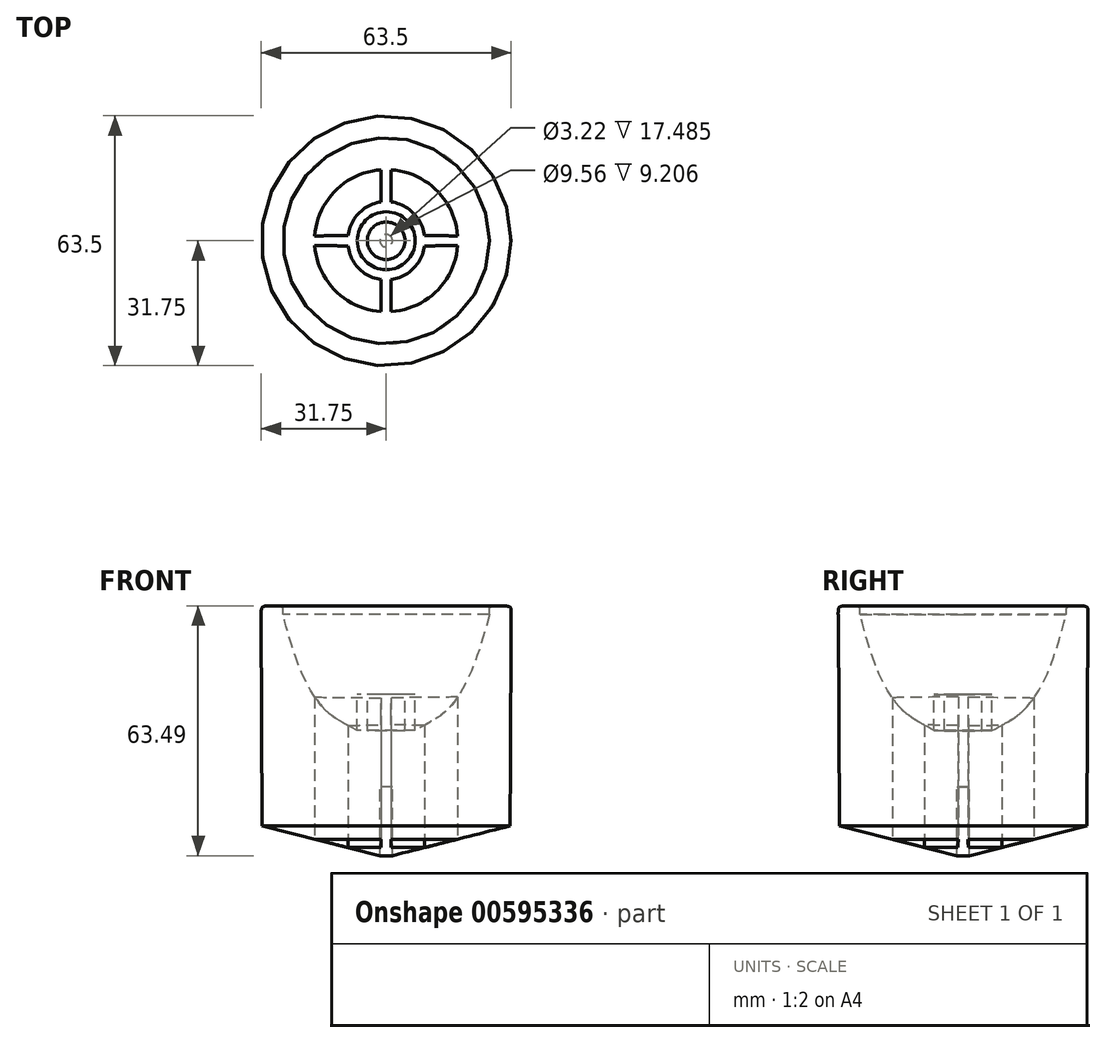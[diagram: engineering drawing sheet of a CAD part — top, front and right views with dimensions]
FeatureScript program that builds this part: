
annotation { "Feature Type Name" : "Feature", "Feature Type Description" : "" }
export const myFeature = defineFeature(function(context is Context, id is Id, definition is map)
    precondition{}
    {
        {
            var Q0;
            Q0=qCreatedBy(makeId("Front.planeOp"),FACE);
            var sketch = newSketch(context, id + "F0", { "sketchPlane" : qUnion([Q0])});
            skLineSegment(sketch, "E0", {"start": v(1.6, 0) * mm, "end": v(31.48, 7.57) * mm});
            skLineSegment(sketch, "E1", {"start": v(0, 31.74) * mm, "end": v(4.78, 31.74) * mm});
            skLineSegment(sketch, "E2", {"start": v(4.78, 31.74) * mm, "end": v(4.78, 40.95) * mm});
            skLineSegment(sketch, "E3", {"start": v(1.6, 0) * mm, "end": v(1.6, 17.48) * mm});
            skLineSegment(sketch, "E4", {"start": v(1.6, 17.48) * mm, "end": v(0, 17.48) * mm});
            skLineSegment(sketch, "E5", {"start": v(0, 31.74) * mm, "end": v(0, 17.48) * mm});
            skLineSegment(sketch, "E6", {"start": v(4.78, 40.95) * mm, "end": v(7.36, 40.95) * mm});
            skLineSegment(sketch, "E7", {"start": v(7.36, 40.95) * mm, "end": v(7.36, 31.8) * mm});
            skPoint(sketch, "E8.2.internal.snap0", {"position": v(28.98, 63.49) * mm});
            skFitSpline(sketch, "E9", {"points": [v(26.2, 61.3) * mm, v(26.51, 63.2) * mm, v(28.98, 63.49) * mm, v(31.32, 63.24) * mm, v(31.75, 61.2) * mm], "startDerivative": vector(0.04, 14) * mm, "endDerivative": vector(-0.08, -17.1) * mm});
            skLineSegment(sketch, "E10", {"start": v(31.75, 61.2) * mm, "end": v(31.48, 7.57) * mm});
            skFitSpline(sketch, "E11", {"points": [v(26.2, 61.3) * mm, v(15.77, 37.33) * mm, v(7.36, 31.8) * mm], "startDerivative": vector(-18.03, -70.82) * mm, "endDerivative": vector(-34.13, -18.42) * mm});
            skSolve(sketch);
        }
        {
            var Q0;
            Q0=makeQuery(id+"F0.imprint","IMPRINT",FACE,{"disambiguationData":[TD([[makeQuery(id+"F0.imprint","IMPRINT",EDGE,{"derivedFrom":sQuery(id+"F0.wireOp",EDGE,"E0")}),1.0]])]});
            var Q1;
            Q1=sQuery(id+"F0.wireOp",EDGE,"E5");
            revolve(context, id + "F1", {"entities" : qUnion([Q0]), "axis" : qUnion([Q1]), "revolveType" : RevolveType.FULL});
        }
        {
            var Q0;
            Q0=qCreatedBy(makeId("Top.planeOp"),FACE);
            var sketch = newSketch(context, id + "F2", { "sketchPlane" : qUnion([Q0])});
            skLineSegment(sketch, "E12", {"start": v(-13.94, 1.27) * mm, "end": v(-9.7, 1.3) * mm});
            skLineSegment(sketch, "E13", {"start": v(-1.27, 9.88) * mm, "end": v(-1.27, 13.95) * mm});
            skLineSegment(sketch, "E14", {"start": v(-13.94, 1.27) * mm, "end": v(-18.17, 1.24) * mm});
            skLineSegment(sketch, "E15", {"start": v(-1.27, 13.95) * mm, "end": v(-1.27, 18) * mm});
            skPoint(sketch, "E15.endSnap0", {"position": v(-1.27, 11.91) * mm});
            skArc(sketch, "E16", {"start": v(-1.27, 9.88) * mm, "mid": v(-6.95, 7.02) * mm, "end": v(-9.7, 1.3) * mm});
            skArc(sketch, "E17", {"start": v(-1.27, 18) * mm, "mid": v(-12.85, 12.78) * mm, "end": v(-18.17, 1.24) * mm});
            skLineSegment(sketch, "E18.MirrorCS", {"start": v(1.27, 13.95) * mm, "end": v(1.27, 18) * mm});
            skLineSegment(sketch, "E19.MirrorCS", {"start": v(1.27, 9.88) * mm, "end": v(1.27, 13.95) * mm});
            skArc(sketch, "E20.MirrorCS", {"start": v(1.27, 18) * mm, "mid": v(12.85, 12.78) * mm, "end": v(18.17, 1.24) * mm});
            skArc(sketch, "E21.MirrorCS", {"start": v(1.27, 9.88) * mm, "mid": v(6.95, 7.02) * mm, "end": v(9.7, 1.3) * mm});
            skLineSegment(sketch, "E22.MirrorCS", {"start": v(13.94, 1.27) * mm, "end": v(9.7, 1.3) * mm});
            skLineSegment(sketch, "E23.MirrorCS", {"start": v(13.94, 1.27) * mm, "end": v(18.17, 1.24) * mm});
            skArc(sketch, "E24.MirrorCS", {"start": v(-1.27, -9.88) * mm, "mid": v(-6.95, -7.02) * mm, "end": v(-9.7, -1.3) * mm});
            skLineSegment(sketch, "E25.MirrorCS", {"start": v(-13.94, -1.27) * mm, "end": v(-9.7, -1.3) * mm});
            skLineSegment(sketch, "E26.MirrorCS", {"start": v(-13.94, -1.27) * mm, "end": v(-18.17, -1.24) * mm});
            skArc(sketch, "E27.MirrorCS", {"start": v(-1.27, -18) * mm, "mid": v(-12.85, -12.78) * mm, "end": v(-18.17, -1.24) * mm});
            skLineSegment(sketch, "E28.MirrorCS", {"start": v(-1.27, -13.95) * mm, "end": v(-1.27, -18) * mm});
            skLineSegment(sketch, "E29.MirrorCS", {"start": v(-1.27, -9.88) * mm, "end": v(-1.27, -13.95) * mm});
            skLineSegment(sketch, "E30.MirrorCS", {"start": v(1.27, -9.88) * mm, "end": v(1.27, -13.95) * mm});
            skLineSegment(sketch, "E31.MirrorCS", {"start": v(1.27, -13.95) * mm, "end": v(1.27, -18) * mm});
            skArc(sketch, "E32.MirrorCS", {"start": v(1.27, -18) * mm, "mid": v(12.85, -12.78) * mm, "end": v(18.17, -1.24) * mm});
            skLineSegment(sketch, "E33.MirrorCS", {"start": v(13.94, -1.27) * mm, "end": v(18.17, -1.24) * mm});
            skLineSegment(sketch, "E34.MirrorCS", {"start": v(13.94, -1.27) * mm, "end": v(9.7, -1.3) * mm});
            skArc(sketch, "E35.MirrorCS", {"start": v(1.27, -9.88) * mm, "mid": v(6.95, -7.02) * mm, "end": v(9.7, -1.3) * mm});
            skSolve(sketch);
        }
        {
            var Q0;
            Q0 = qSketchRegion(id + "F2", true);
            extrude(context, id + "F3", {"entities" : qUnion([Q0]), "operationType" : NewBodyOperationType.REMOVE, "depth" : 44.45 * mm, "offsetDistance" : 25.4 * mm});
        }
    });
